# Revit family: 55555555555
name_source: partatom
category: Plumbing Fixtures
units: mm (PartAtom-declared; Revit-internal decimal feet)

## family parameters
Cut with Voids When Loaded = No
Host = Face
OmniClass Number = 23.45.55.14
OmniClass Title = Single Faucets
Part Type = Normal
Room Calculation Point = No
Round Connector Dimension = Use Diameter
Shared = No

## types (7) — shared parameters
Assembly Code = D2010
CW Connection = Yes
CWFU = 1.5
Cold Water Connection Diameter = 0"
Default Elevation = 0"
Depth = 6 1/2"
Edition number = 1
HW Connection = Yes
HWFU = 1.5
Height = 6 1/2"
Hot Water Connection Diameter = 0"
Keynote = 15410
Manufacturer = Sloan Valve
Product Material = Sloan Valve - Finish - Polished Chrome
Product data url = https://bimobject.com
URL = www.sloanvalve.com
Valve Pressure Drop = 0.00 psi
Vent Connection = No
Waste Connection = No
z_Trim Plate 8 = No
zero-valued in all types: WFU

## per-type parameters (varying)
| type | Description | Part Number | Water Flow | Width | z_No Trim Plate | z_Trim Plate 4 | z_Trim Plate Length |
| EFX-277-4-SOL-ISM-CP-0.5GPM-MLM-IR-FCT | 4" Trim Plate, Solar Power Supply, Integrated Side Mixer, Polished Chrome Finish, 0.5 gpm, Multi-Laminar Spray, Infrared Sensor, BASYS® Solar-Powered Deck-Mounted Mid Body Guided Handwashing Display Faucet. | 3324059 | 1 GPM | 6 1/8" | No | Yes | 6 1/8" |
| EFX-277-4-SOL-ISM-CP-1.5GPM-IR-FCT | 4" Trim Plate, Solar Power Supply, Integrated Side Mixer, Polished Chrome Finish, 1.5 gpm, Aerated (installed) or Laminar (in box) Spray, Infrared Sensor, BASYS® Solar-Powered Deck-Mounted Mid Body Guided Handwashing Display Faucet. | 3324043 | 2 GPM | 6 1/8" | No | Yes | 6 1/8" |
| EFX-277-4-SOL-TEE-CP-0.5GPM-MLM-IR-FCT | 4" Trim Plate, Solar Power Supply, Back-Check Tee, Polished Chrome Finish, 0.5 gpm, Multi-Laminar Spray, Infrared Sensor, BASYS® SolarPowered Deck-Mounted Mid Body Guided Handwashing Display Faucet. | 3324208 | 1 GPM | 6 1/8" | No | Yes | 6 1/8" |
| EFX-277-SOL-ISM-CP-0.5GPM-MLM-IR-FCT | Solar Power Supply, Integrated Side Mixer, Polished Chrome Finish, 0.5 gpm, Multi-Laminar Spray, Infrared Sensor, BASYS® SolarPowered Deck-Mounted Mid Body Guided Handwashing Display Faucet. | 3324061 | 1 GPM | 2 1/4" | Yes | No | 5" |
| EFX-277-SOL-ISM-CP-1.5GPM-IR-FCT | Solar Power Supply, Integrated Side Mixer, Polished Chrome Finish, 1.5 gpm, Aerated (installed) or Laminar (in box) Spray, Infrared Sensor, BASYS® Solar-Powered Deck-Mounted Mid Body Guided Handwashing Display Faucet. | 3324032 | 2 GPM | 2 1/4" | Yes | No | 5" |
| EFX-277-SOL-TEE-CP-0.5GPM-MLM-IR-FCT | Solar Power Supply, Back-Check Tee, Polished Chrome Finish, 0.5 gpm, Multi-Laminar Spray, Infrared Sensor, BASYS® Solar-Powered Deck-Mounted Mid Body Guided Handwashing Display Faucet. | 3324213 | 1 GPM | 2 1/4" | Yes | No | 5" |
| EFX-277-SOL-TEE-CP-1.5GPM-IR-FCT | Solar Power Supply, Back-Check Tee, Polished Chrome Finish, 1.5 gpm, Aerated (installed) or Laminar (in box) Spray, Infrared Sensor, BASYS® Solar-Powered Deck-Mounted Mid Body Guided Handwashing Display Faucet. | 3324080 | 2 GPM | 2 1/4" | Yes | No | 5" |

note: column(s) folded — value = type name in every type: Model

## geometry (parser evidence)
native form markers: Sweep x8
no freeform markers — native parametric forms only
